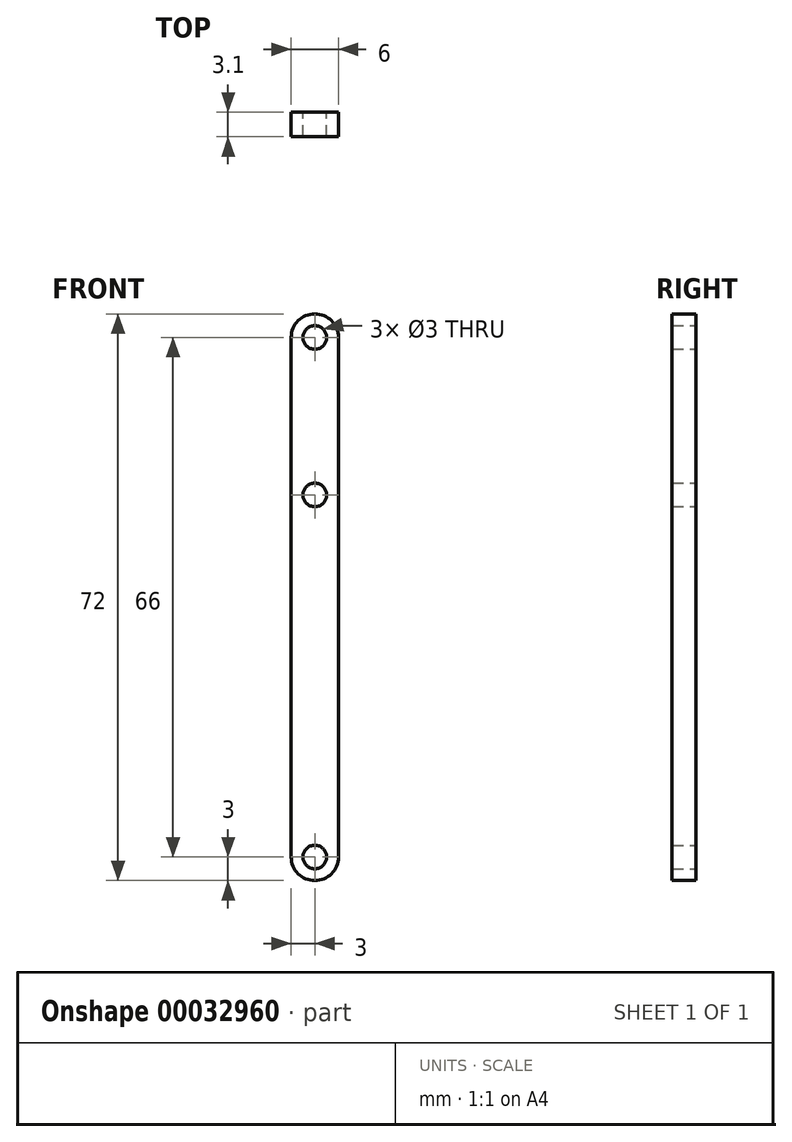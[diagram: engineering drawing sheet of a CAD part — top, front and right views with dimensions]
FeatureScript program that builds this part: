
annotation { "Feature Type Name" : "Feature", "Feature Type Description" : "" }
export const myFeature = defineFeature(function(context is Context, id is Id, definition is map)
    precondition{}
    {
        {
            var Q0;
            Q0=qCreatedBy(makeId("Front.planeOp"),FACE);
            var sketch = newSketch(context, id + "F0", { "sketchPlane" : qUnion([Q0])});
            skCircle(sketch, "E0", {"center": v(0, 33) * mm, "radius": 1.5 * mm});
            skCircle(sketch, "E1.MirrorC", {"center": v(0, -33) * mm, "radius": 1.5 * mm});
            skArc(sketch, "E2", {"start": v(3, 33) * mm, "mid": v(0, 36) * mm, "end": v(-3, 33) * mm});
            skLineSegment(sketch, "E3", {"start": v(0, 33) * mm, "end": v(3, 33) * mm, "construction": true});
            skLineSegment(sketch, "E4", {"start": v(3, 33) * mm, "end": v(3, 0) * mm});
            skLineSegment(sketch, "E5.MirrorCS", {"start": v(-3, 33) * mm, "end": v(-3, 0) * mm});
            skLineSegment(sketch, "E6.MirrorCS", {"start": v(-3, -33) * mm, "end": v(-3, 0) * mm});
            skLineSegment(sketch, "E7.MirrorCS", {"start": v(3, -33) * mm, "end": v(3, 0) * mm});
            skArc(sketch, "E8.MirrorCS", {"start": v(3, -33) * mm, "mid": v(0, -36) * mm, "end": v(-3, -33) * mm});
            skCircle(sketch, "E9", {"center": v(0, 13) * mm, "radius": 1.5 * mm});
            skSolve(sketch);
        }
        {
            var Q0;
            Q0=qSketchRegion(id+"F0",true);
            extrude(context, id + "F1", {"entities" : qUnion([Q0]), "depth" : 3.1 * mm});
        }
    });
